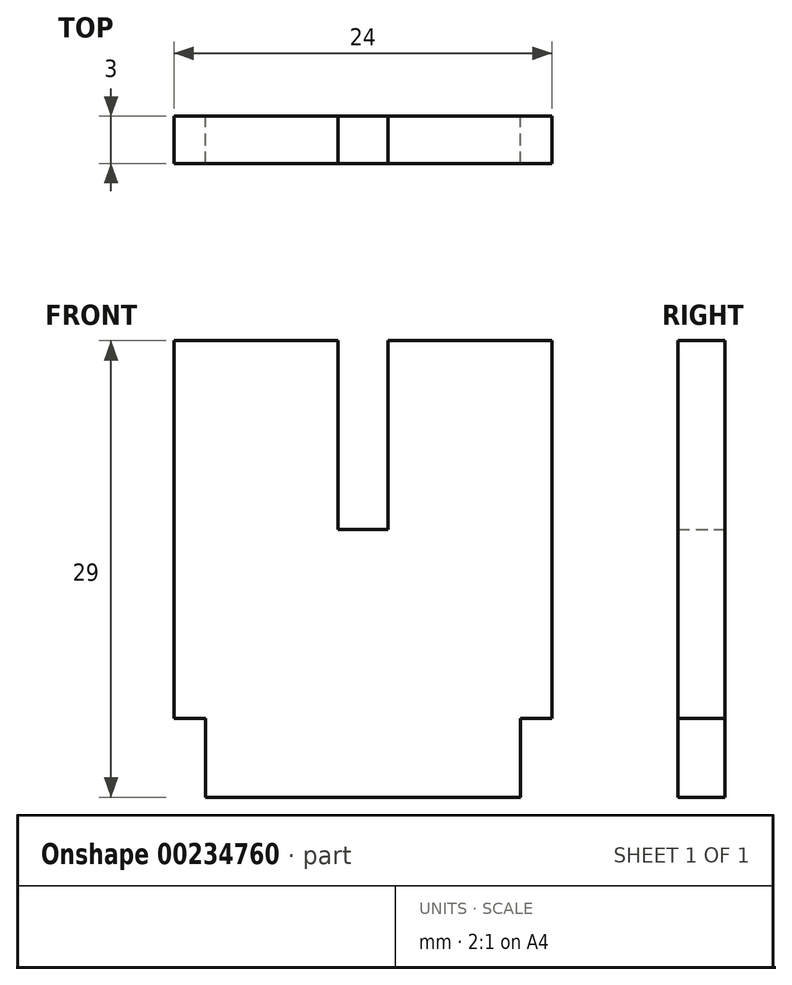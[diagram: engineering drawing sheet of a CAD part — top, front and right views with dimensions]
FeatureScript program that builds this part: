
annotation { "Feature Type Name" : "Feature", "Feature Type Description" : "" }
export const myFeature = defineFeature(function(context is Context, id is Id, definition is map)
    precondition{}
    {
        {
            var Q0;
            Q0=qCreatedBy(makeId("Front.planeOp"),FACE);
            var sketch = newSketch(context, id + "F0", { "sketchPlane" : qUnion([Q0])});
            skLineSegment(sketch, "E0.top", {"start": v(-12, -12) * mm, "end": v(12, -12) * mm});
            skLineSegment(sketch, "E0.left", {"start": v(-12, 12) * mm, "end": v(-12, -12) * mm});
            skLineSegment(sketch, "E0.right", {"start": v(12, 12) * mm, "end": v(12, -12) * mm});
            skPoint(sketch, "E0.middle", {"position": v(0, 0) * mm});
            skLineSegment(sketch, "E1.top", {"start": v(-1.6, 0) * mm, "end": v(1.6, 0) * mm});
            skLineSegment(sketch, "E1.left", {"start": v(-1.6, 12) * mm, "end": v(-1.6, 0) * mm});
            skLineSegment(sketch, "E1.right", {"start": v(1.6, 12) * mm, "end": v(1.6, 0) * mm});
            skLineSegment(sketch, "E2", {"start": v(-12, 12) * mm, "end": v(-1.6, 12) * mm});
            skLineSegment(sketch, "E3", {"start": v(1.6, 12) * mm, "end": v(12, 12) * mm});
            skLineSegment(sketch, "E4.bottom", {"start": v(-10, -12) * mm, "end": v(10, -12) * mm});
            skLineSegment(sketch, "E4.top", {"start": v(-10, -17) * mm, "end": v(10, -17) * mm});
            skLineSegment(sketch, "E4.left", {"start": v(-10, -12) * mm, "end": v(-10, -17) * mm});
            skLineSegment(sketch, "E4.right", {"start": v(10, -12) * mm, "end": v(10, -17) * mm});
            skSolve(sketch);
        }
        {
            var Q0;
            Q0 = qSketchRegion(id + "F0", true);
            extrude(context, id + "F1", {"entities" : qUnion([Q0]), "depth" : 3 * mm});
        }
    });
